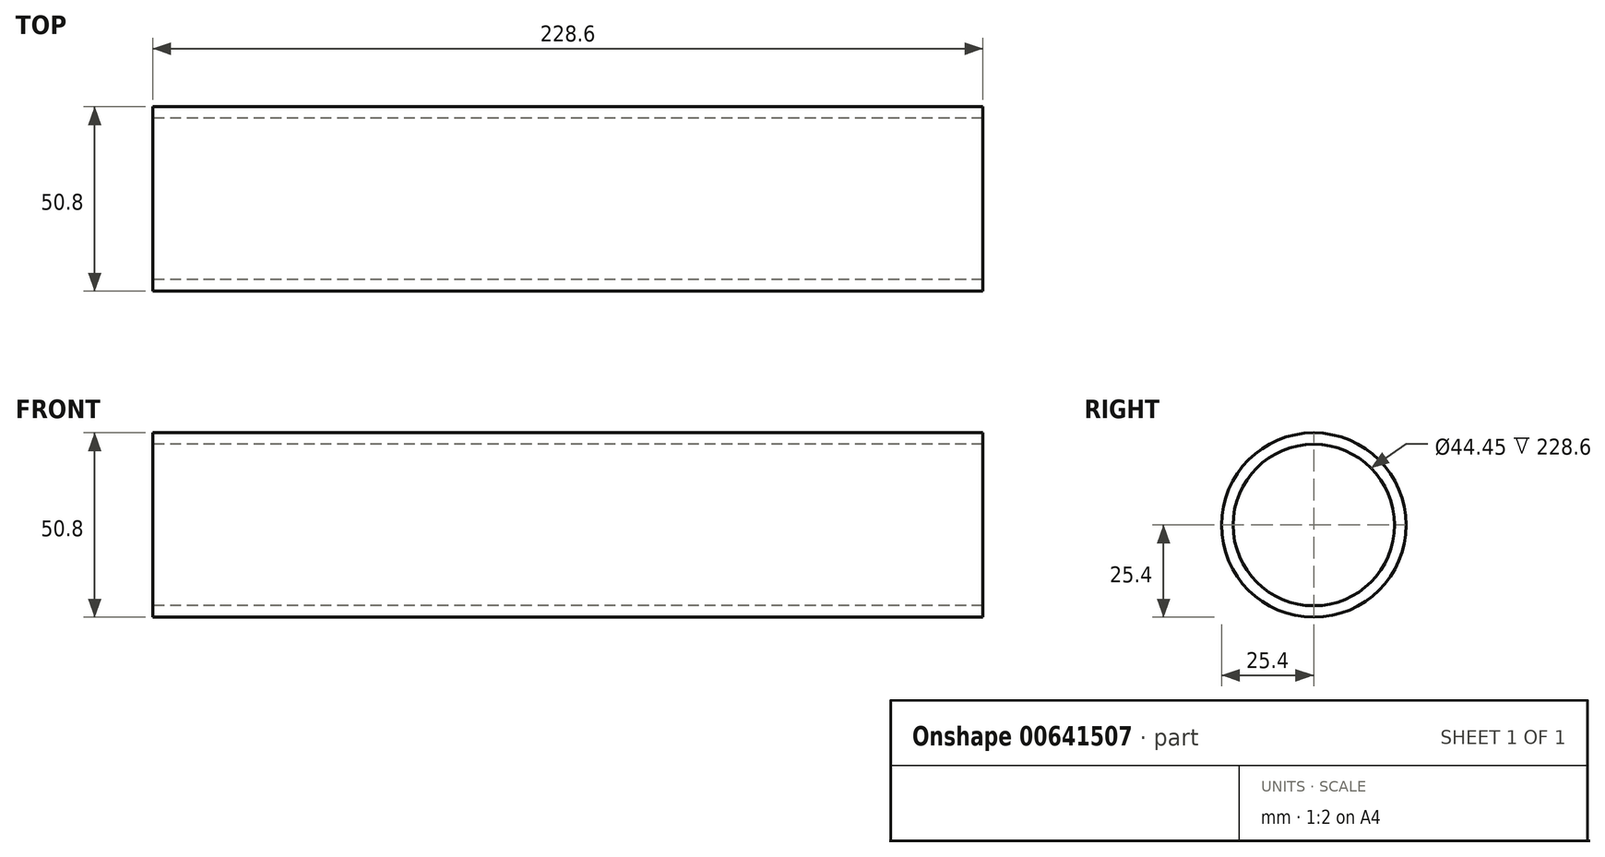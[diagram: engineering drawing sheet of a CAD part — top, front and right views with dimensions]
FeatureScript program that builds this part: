
annotation { "Feature Type Name" : "Feature", "Feature Type Description" : "" }
export const myFeature = defineFeature(function(context is Context, id is Id, definition is map)
    precondition{}
    {
        {
            var Q0;
            Q0=qCreatedBy(makeId("Right.planeOp"),FACE);
            var sketch = newSketch(context, id + "F0", { "sketchPlane" : qUnion([Q0])});
            skCircle(sketch, "E0", {"center": v(0, 0) * mm, "radius": 25.4 * mm});
            skSolve(sketch);
        }
        {
            var Q0;
            Q0=makeQuery(id+"F0.imprint","IMPRINT",FACE,{"disambiguationData":[TD([[makeQuery(id+"F0.imprint","IMPRINT",EDGE,{"derivedFrom":sQuery(id+"F0.wireOp",EDGE,"E0")}),1.0]])]});
            extrude(context, id + "F1", {"entities" : qUnion([Q0]), "depth" : 254 * mm, "offsetDistance" : 25.4 * mm});
        }
        {
            var Q0;
            Q0=makeQuery(id+"F1.opExtrude","CAP_FACE",FACE,{"disambiguationData":[OSD([sQuery(id+"F0.wireOp",EDGE,"E0")])],"isStart":false});
            shell(context, id + "F2", {"entities" : qUnion([Q0]), "thickness" : 3.17 * mm});
        }
        {
            var Q0;
            Q0=makeQuery(id+"F1.opExtrude","CAP_FACE",FACE,{"disambiguationData":[OSD([sQuery(id+"F0.wireOp",EDGE,"E0")])],"isStart":true});
            extrude(context, id + "F3", {"entities" : qUnion([Q0]), "operationType" : NewBodyOperationType.REMOVE, "oppositeDirection" : true, "depth" : 25.4 * mm, "offsetDistance" : 25.4 * mm});
        }
    });
